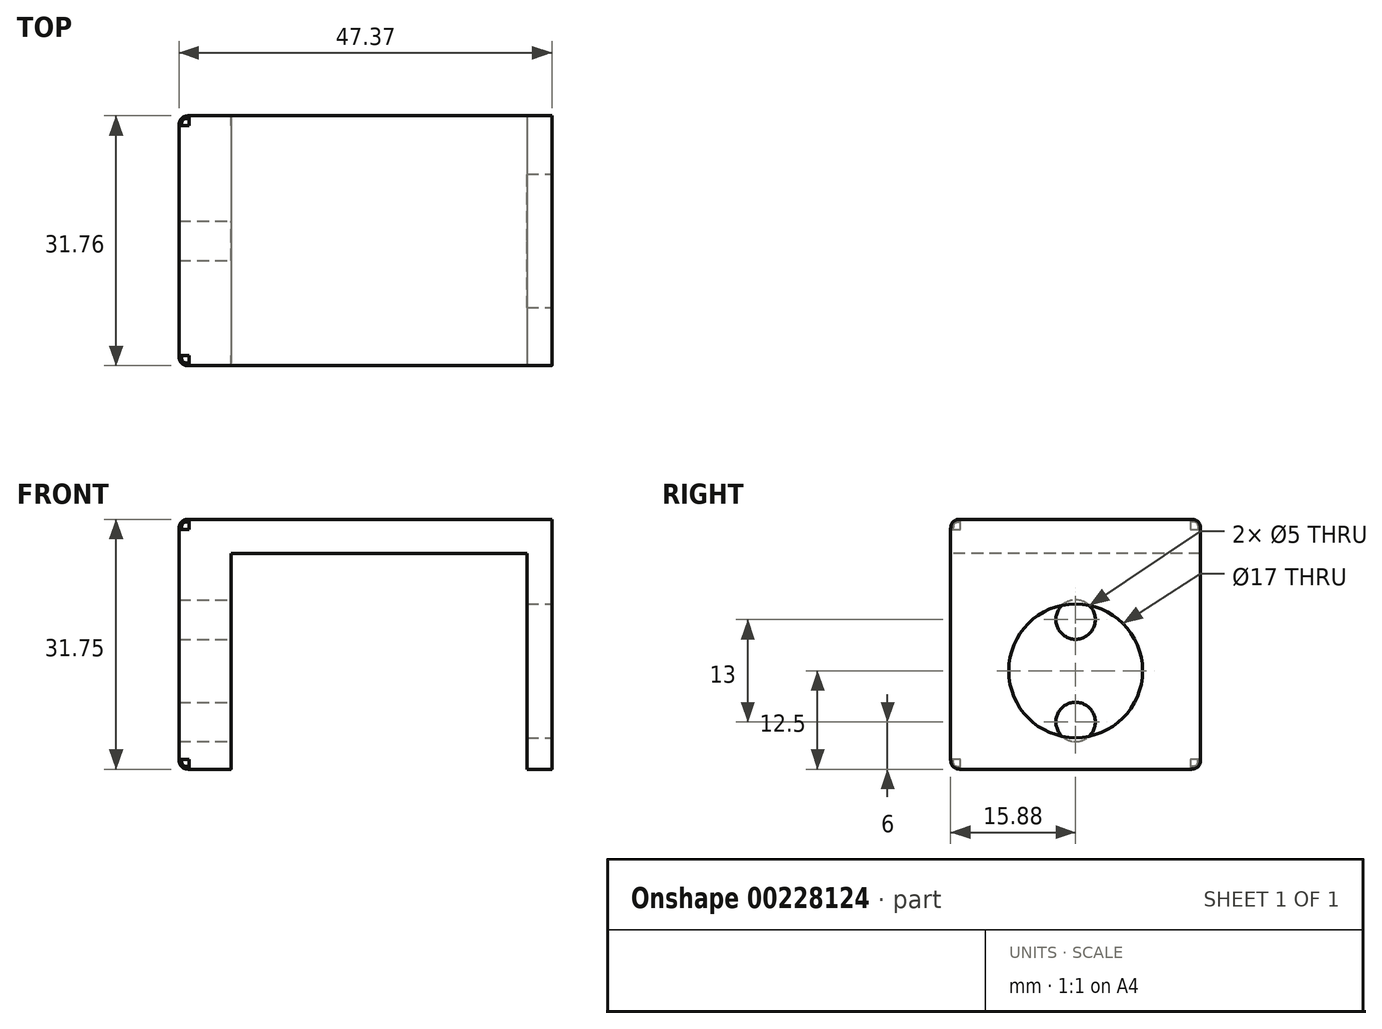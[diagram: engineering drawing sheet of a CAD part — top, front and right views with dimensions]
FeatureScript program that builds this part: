
annotation { "Feature Type Name" : "Feature", "Feature Type Description" : "" }
export const myFeature = defineFeature(function(context is Context, id is Id, definition is map)
    precondition{}
    {
        {
            var Q0;
            Q0=qCreatedBy(makeId("Top.planeOp"),FACE);
            var sketch = newSketch(context, id + "F0", { "sketchPlane" : qUnion([Q0])});
            skLineSegment(sketch, "E0.bottom", {"start": v(-25.4, 15.88) * mm, "end": v(25.4, 15.88) * mm});
            skLineSegment(sketch, "E0.top", {"start": v(-25.4, -15.88) * mm, "end": v(25.4, -15.88) * mm});
            skLineSegment(sketch, "E0.left", {"start": v(-25.4, 15.88) * mm, "end": v(-25.4, -15.87) * mm});
            skLineSegment(sketch, "E0.right", {"start": v(25.4, 15.88) * mm, "end": v(25.4, -15.87) * mm});
            skPoint(sketch, "E0.middle", {"position": v(0, 0) * mm});
            skLineSegment(sketch, "E1.0", {"start": v(-18.8, 15.88) * mm, "end": v(-18.8, -15.87) * mm});
            skLineSegment(sketch, "E2.0", {"start": v(18.8, 15.88) * mm, "end": v(18.8, -15.87) * mm});
            skLineSegment(sketch, "E3.0", {"start": v(21.97, 15.88) * mm, "end": v(21.97, -15.87) * mm});
            skSolve(sketch);
        }
        {
            var Q0;
            Q0=qSketchRegion(id+"F0",true);
            extrude(context, id + "F1", {"entities" : qUnion([Q0]), "depth" : 31.75 * mm});
        }
        {
            var Q0;
            {var subQ0=sQuery(id+"F0.wireOp",EDGE,"E0.right");Q0=makeQuery(id+"F0.imprint","IMPRINT",FACE,{"disambiguationData":[TD([[makeQuery(id+"F0.imprint","IMPRINT",EDGE,{"derivedFrom":subQ0}),-1.0]])]});}
            extrude(context, id + "F2", {"entities" : qUnion([Q0]), "operationType" : NewBodyOperationType.REMOVE, "endBound" : BoundingType.UP_TO_NEXT, "depth" : 25.4 * mm});
        }
        {
            var Q0;
            {var subQ0=sQuery(id+"F0.wireOp",EDGE,"E1.0");Q0=makeQuery(id+"F0.imprint","IMPRINT",FACE,{"disambiguationData":[TD([[makeQuery(id+"F0.imprint","IMPRINT",EDGE,{"derivedFrom":subQ0}),1.0]])]});}
            extrude(context, id + "F3", {"entities" : qUnion([Q0]), "operationType" : NewBodyOperationType.REMOVE, "depth" : 27.43 * mm});
        }
        {
            var Q0;
            Q0=makeQuery(id+"F2.boolean.opBoolean","COPY",FACE,{"derivedFrom":makeQuery(id+"F2.opExtrude","SWEPT_FACE",FACE,{"disambiguationData":[OSD([sQuery(id+"F0.wireOp",EDGE,"E3.0")])]})});
            var sketch = newSketch(context, id + "F4", { "sketchPlane" : qUnion([Q0])});
            skCircle(sketch, "E4", {"center": v(0, 12.5) * mm, "radius": 8.5 * mm});
            skSolve(sketch);
        }
        {
            var Q0;
            Q0=makeQuery(id+"F4.imprint","IMPRINT",FACE,{"disambiguationData":[TD([[makeQuery(id+"F4.imprint","IMPRINT",EDGE,{"derivedFrom":sQuery(id+"F4.wireOp",EDGE,"E4")}),1.0]])]});
            var Q1;
            Q1=sQuery(id+"F4.wireOp",EDGE,"E4");
            extrude(context, id + "F5", {"entities" : qUnion([Q0]), "operationType" : NewBodyOperationType.REMOVE, "surfaceEntities" : qUnion([Q1]), "endBound" : BoundingType.UP_TO_NEXT, "oppositeDirection" : true, "depth" : 25.4 * mm});
        }
        {
            var Q0;
            Q0=makeQuery(id+"F1.opExtrude","SWEPT_FACE",FACE,{"disambiguationData":[OSD([sQuery(id+"F0.wireOp",EDGE,"E0.left")])]});
            var sketch = newSketch(context, id + "F6", { "sketchPlane" : qUnion([Q0])});
            skPoint(sketch, "E5", {"position": v(0, 19) * mm});
            skPoint(sketch, "E6", {"position": v(0, 18.82) * mm});
            skPoint(sketch, "E7", {"position": v(0, 6) * mm});
            skSolve(sketch);
        }
        {
            var Q0;
            Q0=sQuery(id+"F6.wireOp",VERTEX,"E5");
            var Q1;
            Q1=sQuery(id+"F6.wireOp",VERTEX,"E7");
            var Q2;
            Q2=makeQuery(id+"F1.opExtrude","SWEPT_BODY",BODY,{"disambiguationData":[OSD([sQuery(id+"F0.wireOp",EDGE,"E0.bottom"),sQuery(id+"F0.wireOp",EDGE,"E0.top"),sQuery(id+"F0.wireOp",EDGE,"E0.left"),sQuery(id+"F0.wireOp",EDGE,"E0.right")])]});
            hole(context, id + "F7", {"style" : HoleStyle.SIMPLE, "endStyle" : HoleEndStyle.BLIND, "standardTappedOrClearance" : lookupTablePath({ "standard" : "ISO", "engagement" : "75%", "pitch" : "1 mm", "size" : "M6", "type" : "Tapped" }), "standardBlindInLast" : lookupTablePath({ "standard" : "ISO", "engagement" : "75%", "pitch" : "1 mm", "size" : "M6", "type" : "Tapped" }), "holeDiameter" : 5 * mm, "showTappedDepth" : true, "holeDepth" : 10.16 * mm, "tappedDepth" : 10.16 * mm, "tapClearance" : 0, "locations" : qUnion([Q0, Q1]), "scope" : qUnion([Q2]), "majorDiameter" : 6 * mm, "startStyle" : HoleStartStyle.SKETCH});
        }
        {
            var Q0;
            Q0=makeQuery(id+"F2.boolean.opBoolean","COPY",EDGE,{"derivedFrom":makeQuery(id+"F2.opExtrude","CAP_EDGE",EDGE,{"disambiguationData":[OSD([sQuery(id+"F0.wireOp",EDGE,"E3.0")])],"isStart":true})});
            var Q1;
            Q1=makeQuery(id+"F2.boolean.opBoolean","COPY",EDGE,{"derivedFrom":makeQuery(id+"F2.opExtrude","SWEPT_EDGE",EDGE,{"disambiguationData":[OSD([sQuery(id+"F0.wireOp",EDGE,"E0.top"),sQuery(id+"F0.wireOp",EDGE,"E3.0")])]})});
            var Q2;
            Q2=makeQuery(id+"F2.boolean.opBoolean","COPY",EDGE,{"derivedFrom":makeQuery(id+"F2.opExtrude","SWEPT_EDGE",EDGE,{"disambiguationData":[OSD([sQuery(id+"F0.wireOp",EDGE,"E0.bottom"),sQuery(id+"F0.wireOp",EDGE,"E3.0")])]})});
            var Q3;
            Q3=makeQuery(id+"F2.boolean.opBoolean","COPY",EDGE,{"derivedFrom":makeQuery(id+"F2.opExtrude","TWEAK_EDGE",EDGE,{"derivedFrom":[makeQuery(id+"F0.imprint","IMPRINT",EDGE,{"derivedFrom":sQuery(id+"F0.wireOp",EDGE,"E3.0")}),makeQuery(id+"F1.opExtrude","CAP_FACE",FACE,{"disambiguationData":[OSD([sQuery(id+"F0.wireOp",EDGE,"E0.bottom"),sQuery(id+"F0.wireOp",EDGE,"E0.top"),sQuery(id+"F0.wireOp",EDGE,"E0.left"),sQuery(id+"F0.wireOp",EDGE,"E0.right")])],"isStart":false})]})});
            var Q4;
            Q4=makeQuery(id+"F1.opExtrude","CAP_EDGE",EDGE,{"disambiguationData":[OSD([sQuery(id+"F0.wireOp",EDGE,"E0.top")])],"isStart":false});
            var Q5;
            Q5=makeQuery(id+"F1.opExtrude","SWEPT_EDGE",EDGE,{"disambiguationData":[OSD([sQuery(id+"F0.wireOp",EDGE,"E0.top"),sQuery(id+"F0.wireOp",EDGE,"E0.left")])]});
            var Q6;
            Q6=makeQuery(id+"F1.opExtrude","CAP_EDGE",EDGE,{"disambiguationData":[OSD([sQuery(id+"F0.wireOp",EDGE,"E0.left")])],"isStart":false});
            var Q7;
            Q7=makeQuery(id+"F1.opExtrude","CAP_EDGE",EDGE,{"disambiguationData":[OSD([sQuery(id+"F0.wireOp",EDGE,"E0.bottom")])],"isStart":false});
            var Q8;
            {var subQ0=sQuery(id+"F0.wireOp",EDGE,"E0.left");var subQ1=sQuery(id+"F0.wireOp",EDGE,"E0.top");Q8=makeQuery(id+"F3.boolean.opBoolean","SPLIT",EDGE,{"disambiguationData":[TD([makeQuery(id+"F1.opExtrude","SWEPT_FACE",FACE,{"disambiguationData":[OSD([subQ0])]})])],"derivedFrom":makeQuery(id+"F1.opExtrude","CAP_EDGE",EDGE,{"disambiguationData":[OSD([subQ1])],"isStart":true})});}
            var Q9;
            {var subQ0=sQuery(id+"F0.wireOp",EDGE,"E0.top");Q9=makeQuery(id+"F3.boolean.opBoolean","SPLIT",EDGE,{"disambiguationData":[TD([makeQuery(id+"F2.boolean.opBoolean","COPY",FACE,{"derivedFrom":makeQuery(id+"F2.opExtrude","SWEPT_FACE",FACE,{"disambiguationData":[OSD([sQuery(id+"F0.wireOp",EDGE,"E3.0")])]})})])],"derivedFrom":makeQuery(id+"F1.opExtrude","CAP_EDGE",EDGE,{"disambiguationData":[OSD([subQ0])],"isStart":true})});}
            var Q10;
            {var subQ0=sQuery(id+"F0.wireOp",EDGE,"E0.bottom");Q10=makeQuery(id+"F3.boolean.opBoolean","SPLIT",EDGE,{"disambiguationData":[TD([makeQuery(id+"F2.boolean.opBoolean","COPY",FACE,{"derivedFrom":makeQuery(id+"F2.opExtrude","SWEPT_FACE",FACE,{"disambiguationData":[OSD([sQuery(id+"F0.wireOp",EDGE,"E3.0")])]})})])],"derivedFrom":makeQuery(id+"F1.opExtrude","CAP_EDGE",EDGE,{"disambiguationData":[OSD([subQ0])],"isStart":true})});}
            var Q11;
            Q11=makeQuery(id+"F1.opExtrude","SWEPT_EDGE",EDGE,{"disambiguationData":[OSD([sQuery(id+"F0.wireOp",EDGE,"E0.bottom"),sQuery(id+"F0.wireOp",EDGE,"E0.left")])]});
            var Q12;
            {var subQ0=sQuery(id+"F0.wireOp",EDGE,"E0.bottom");var subQ1=sQuery(id+"F0.wireOp",EDGE,"E0.left");Q12=makeQuery(id+"F3.boolean.opBoolean","SPLIT",EDGE,{"disambiguationData":[TD([makeQuery(id+"F1.opExtrude","SWEPT_FACE",FACE,{"disambiguationData":[OSD([subQ1])]})])],"derivedFrom":makeQuery(id+"F1.opExtrude","CAP_EDGE",EDGE,{"disambiguationData":[OSD([subQ0])],"isStart":true})});}
            var Q13;
            Q13=makeQuery(id+"F1.opExtrude","CAP_EDGE",EDGE,{"disambiguationData":[OSD([sQuery(id+"F0.wireOp",EDGE,"E0.left")])],"isStart":true});
            fillet(context, id + "F8", {"entities" : qUnion([Q0, Q1, Q2, Q3, Q4, Q5, Q6, Q7, Q8, Q9, Q10, Q11, Q12, Q13]), "radius" : 1.27 * mm, "rho" : 0.5, "crossSection" : FilletCrossSection.CONIC, "allowEdgeOverflow" : false});
        }
    });
